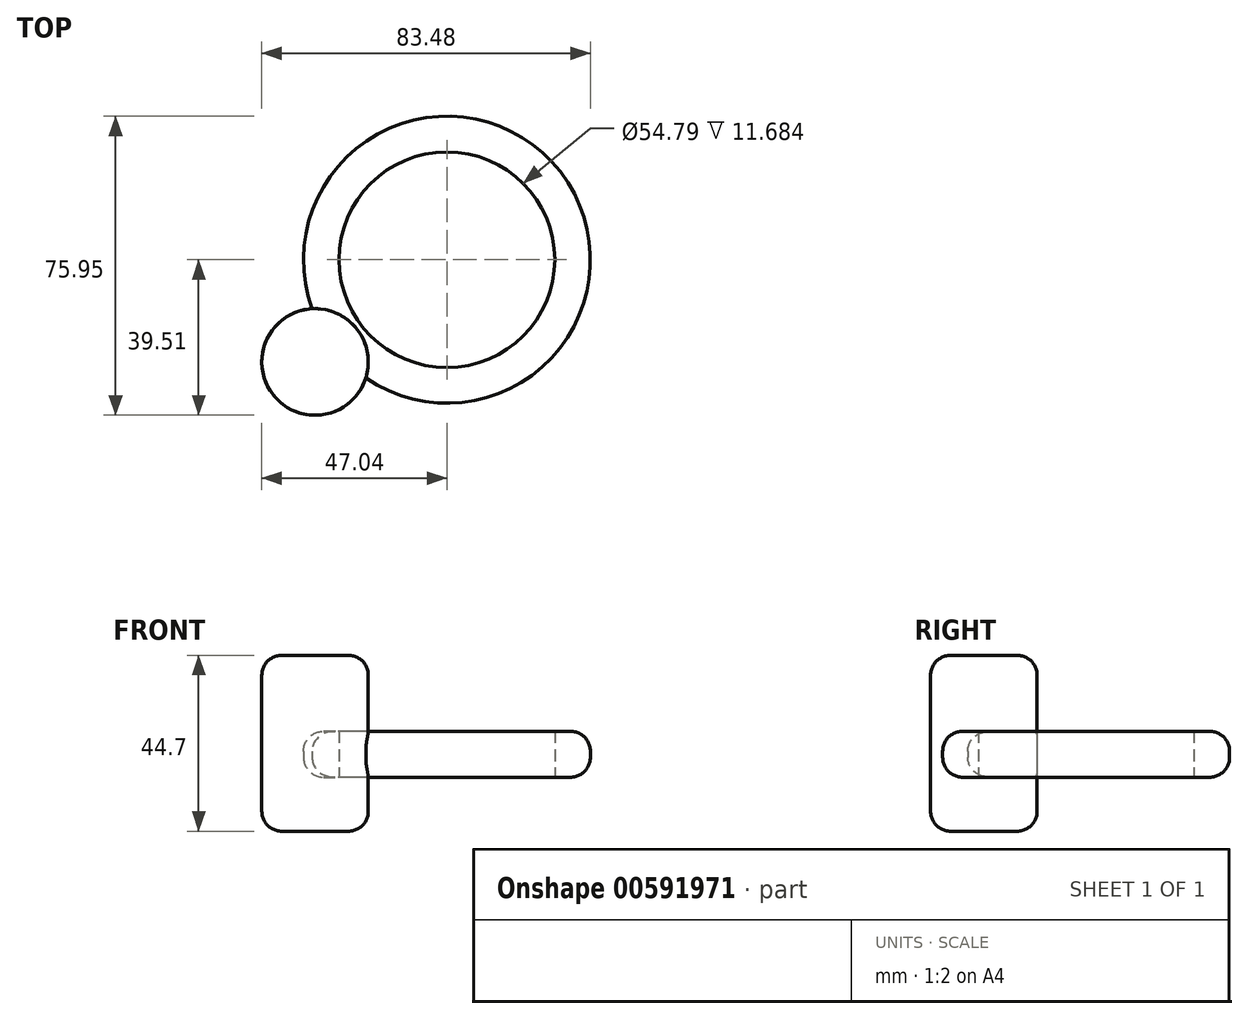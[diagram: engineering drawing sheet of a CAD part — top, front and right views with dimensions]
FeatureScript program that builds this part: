
annotation { "Feature Type Name" : "Feature", "Feature Type Description" : "" }
export const myFeature = defineFeature(function(context is Context, id is Id, definition is map)
    precondition{}
    {
        {
            var Q0;
            Q0=qCreatedBy(makeId("Top.planeOp"),FACE);
            var sketch = newSketch(context, id + "F0", { "sketchPlane" : qUnion([Q0])});
            skCircle(sketch, "E0", {"center": v(0, 0) * mm, "radius": 36.44 * mm});
            skCircle(sketch, "E1", {"center": v(0, 0) * mm, "radius": 27.4 * mm});
            skSolve(sketch);
        }
        {
            var Q0;
            Q0 = qSketchRegion(id + "F0", true);
            extrude(context, id + "F1", {"entities" : qUnion([Q0]), "depth" : 6.1 * mm, "offsetDistance" : 25.4 * mm});
        }
        {
            var Q0;
            Q0=qCreatedBy(makeId("Top.planeOp"),FACE);
            var sketch = newSketch(context, id + "F2", { "sketchPlane" : qUnion([Q0])});
            skCircle(sketch, "E2", {"center": v(-33.5, -25.98) * mm, "radius": 13.53 * mm});
            skSolve(sketch);
        }
        {
            var Q0;
            Q0 = qSketchRegion(id + "F2", true);
            extrude(context, id + "F3", {"entities" : qUnion([Q0]), "operationType" : NewBodyOperationType.ADD, "depth" : 25.4 * mm, "offsetDistance" : 25.4 * mm, "hasSecondDirection" : true, "secondDirectionOppositeDirection" : true, "secondDirectionDepth" : 19.3 * mm});
        }
        {
            var Q0;
            Q0=makeQuery(id+"F3.opExtrude","CAP_EDGE",EDGE,{"disambiguationData":[OSD([sQuery(id+"F2.wireOp",EDGE,"E2")])],"isStart":false});
            var Q1;
            Q1=makeQuery(id+"F3.opExtrude","CAP_EDGE",EDGE,{"disambiguationData":[OSD([sQuery(id+"F2.wireOp",EDGE,"E2")])],"isStart":true});
            fillet(context, id + "F4", {"entities" : qUnion([Q0, Q1]), "radius" : 5.08 * mm, "tangentPropagation" : true, "allowEdgeOverflow" : false});
        }
        {
            var Q0;
            Q0=makeQuery(id+"F1.opExtrude","CAP_FACE",FACE,{"disambiguationData":[OSD([sQuery(id+"F0.wireOp",EDGE,"E0"),sQuery(id+"F0.wireOp",EDGE,"E1")])],"isStart":false});
            extrude(context, id + "F5", {"entities" : qUnion([Q0]), "operationType" : NewBodyOperationType.ADD, "oppositeDirection" : true, "depth" : 11.68 * mm, "offsetDistance" : 25.4 * mm});
        }
        {
            var Q0;
            Q0=makeQuery(id+"F1.opExtrude","CAP_EDGE",EDGE,{"disambiguationData":[OSD([sQuery(id+"F0.wireOp",EDGE,"E0")])],"isStart":false});
            var Q1;
            Q1=makeQuery(id+"F5.opExtrude","CAP_EDGE",EDGE,{"disambiguationData":[OSD([sQuery(id+"F0.wireOp",EDGE,"E0")])],"isStart":false});
            fillet(context, id + "F6", {"entities" : qUnion([Q0, Q1]), "radius" : 5.08 * mm, "tangentPropagation" : true, "allowEdgeOverflow" : false});
        }
    });
